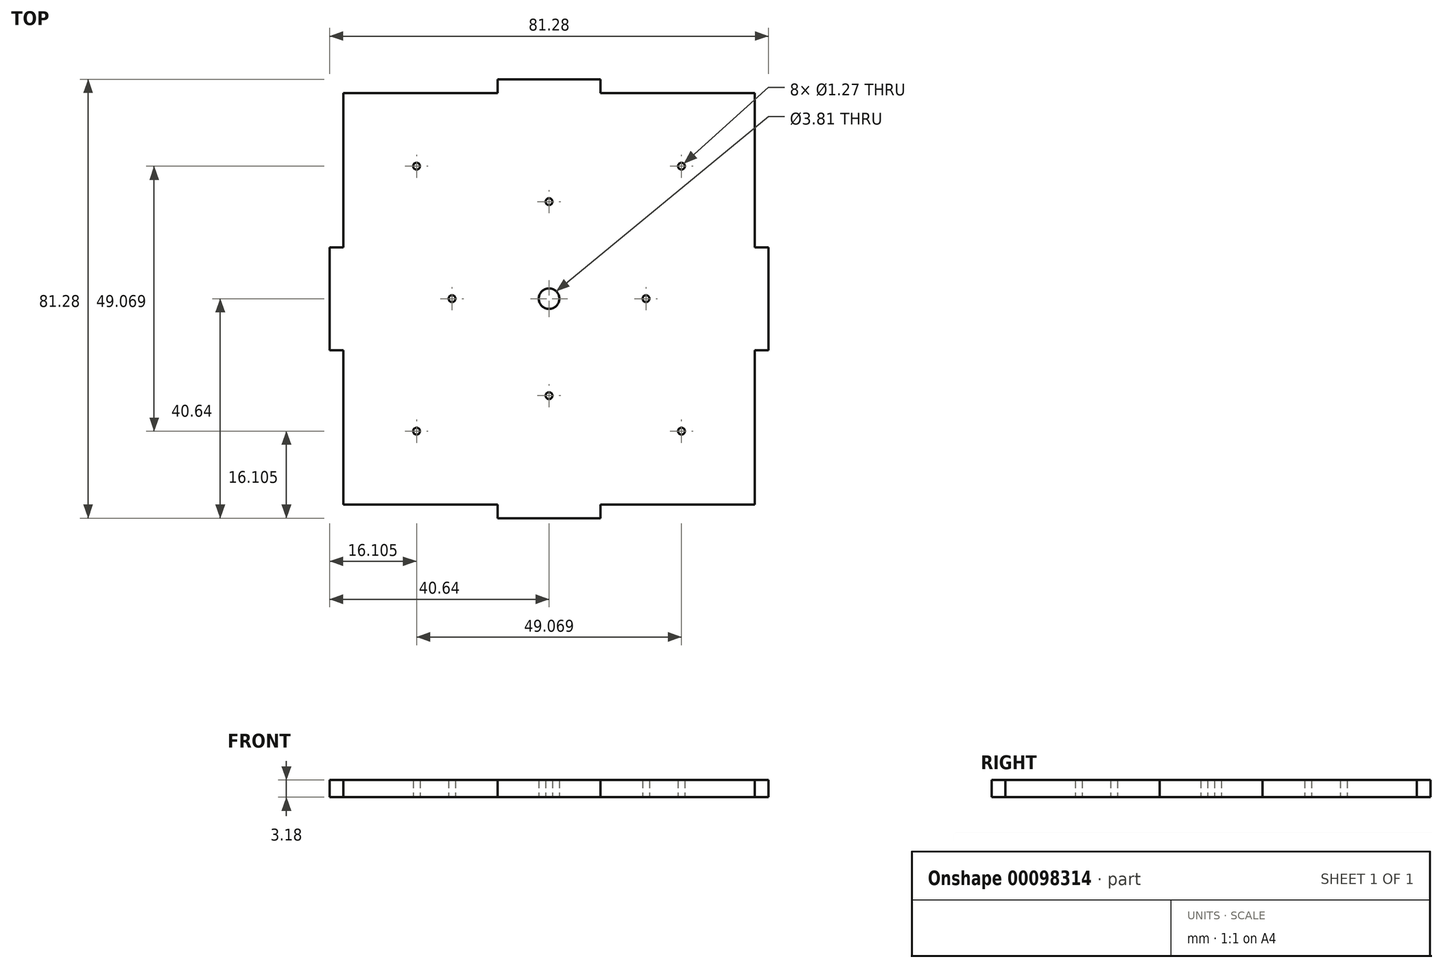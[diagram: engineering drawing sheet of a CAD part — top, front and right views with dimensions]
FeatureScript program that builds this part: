
annotation { "Feature Type Name" : "Feature", "Feature Type Description" : "" }
export const myFeature = defineFeature(function(context is Context, id is Id, definition is map)
    precondition{}
    {
        {
            var Q0;
            Q0=qCreatedBy(makeId("Top.planeOp"),FACE);
            var sketch = newSketch(context, id + "F0", { "sketchPlane" : qUnion([Q0])});
            skCircle(sketch, "E0", {"center": v(0, 17.96) * mm, "radius": 6.99 * mm, "construction": true});
            skCircle(sketch, "E1", {"center": v(-17.96, 0) * mm, "radius": 6.99 * mm, "construction": true});
            skCircle(sketch, "E2", {"center": v(0, -17.96) * mm, "radius": 6.99 * mm, "construction": true});
            skCircle(sketch, "E3", {"center": v(17.96, 0) * mm, "radius": 6.99 * mm, "construction": true});
            skCircle(sketch, "E4", {"center": v(24.53, 24.53) * mm, "radius": 6.99 * mm, "construction": true});
            skCircle(sketch, "E5", {"center": v(-24.53, 24.53) * mm, "radius": 6.99 * mm, "construction": true});
            skCircle(sketch, "E6", {"center": v(-24.53, -24.53) * mm, "radius": 6.99 * mm, "construction": true});
            skCircle(sketch, "E7", {"center": v(24.53, -24.53) * mm, "radius": 6.99 * mm, "construction": true});
            skLineSegment(sketch, "E8", {"start": v(-17.96, 0) * mm, "end": v(0, 17.96) * mm, "construction": true});
            skLineSegment(sketch, "E9", {"start": v(17.96, 0) * mm, "end": v(0, 17.96) * mm, "construction": true});
            skLineSegment(sketch, "E10", {"start": v(0, -17.96) * mm, "end": v(-17.96, 0) * mm, "construction": true});
            skLineSegment(sketch, "E11", {"start": v(0, -17.96) * mm, "end": v(17.96, 0) * mm, "construction": true});
            skLineSegment(sketch, "E12", {"start": v(-24.53, -24.53) * mm, "end": v(24.53, 24.53) * mm, "construction": true});
            skLineSegment(sketch, "E13", {"start": v(-24.53, 24.53) * mm, "end": v(24.53, -24.53) * mm, "construction": true});
            skLineSegment(sketch, "E14", {"start": v(0, 17.96) * mm, "end": v(24.53, 24.53) * mm, "construction": true});
            skLineSegment(sketch, "E15", {"start": v(-38.1, 38.1) * mm, "end": v(-9.53, 38.1) * mm});
            skLineSegment(sketch, "E16", {"start": v(-9.52, 38.1) * mm, "end": v(-9.52, 40.64) * mm});
            skLineSegment(sketch, "E17", {"start": v(-9.53, 40.64) * mm, "end": v(9.52, 40.64) * mm});
            skLineSegment(sketch, "E18", {"start": v(9.53, 40.64) * mm, "end": v(9.53, 38.1) * mm});
            skLineSegment(sketch, "E19", {"start": v(9.53, 38.1) * mm, "end": v(38.1, 38.1) * mm});
            skLineSegment(sketch, "E20", {"start": v(38.1, 38.1) * mm, "end": v(38.1, 9.53) * mm});
            skLineSegment(sketch, "E21", {"start": v(38.1, 9.53) * mm, "end": v(40.64, 9.53) * mm});
            skLineSegment(sketch, "E22", {"start": v(40.64, 9.53) * mm, "end": v(40.64, -9.52) * mm});
            skLineSegment(sketch, "E23", {"start": v(40.64, -9.52) * mm, "end": v(38.1, -9.52) * mm});
            skLineSegment(sketch, "E24", {"start": v(38.1, -9.52) * mm, "end": v(38.1, -38.1) * mm});
            skLineSegment(sketch, "E25", {"start": v(38.1, -38.1) * mm, "end": v(9.53, -38.1) * mm});
            skLineSegment(sketch, "E26", {"start": v(9.53, -38.1) * mm, "end": v(9.53, -40.64) * mm});
            skLineSegment(sketch, "E27", {"start": v(9.52, -40.64) * mm, "end": v(-9.53, -40.64) * mm});
            skLineSegment(sketch, "E28", {"start": v(-9.52, -40.64) * mm, "end": v(-9.52, -38.1) * mm});
            skLineSegment(sketch, "E29", {"start": v(-9.53, -38.1) * mm, "end": v(-38.1, -38.1) * mm});
            skLineSegment(sketch, "E30", {"start": v(-38.1, -38.1) * mm, "end": v(-38.1, -9.52) * mm});
            skLineSegment(sketch, "E31", {"start": v(-38.1, -9.52) * mm, "end": v(-40.64, -9.52) * mm});
            skLineSegment(sketch, "E32", {"start": v(-40.64, -9.52) * mm, "end": v(-40.64, 9.53) * mm});
            skLineSegment(sketch, "E33", {"start": v(-40.64, 9.53) * mm, "end": v(-38.1, 9.53) * mm});
            skLineSegment(sketch, "E34", {"start": v(-38.1, 9.53) * mm, "end": v(-38.1, 38.1) * mm});
            skCircle(sketch, "E35", {"center": v(0, 0) * mm, "radius": 1.9 * mm});
            skCircle(sketch, "E36", {"center": v(-24.53, 24.53) * mm, "radius": 0.64 * mm});
            skCircle(sketch, "E37", {"center": v(0, 17.96) * mm, "radius": 0.64 * mm});
            skCircle(sketch, "E38", {"center": v(24.53, 24.53) * mm, "radius": 0.64 * mm});
            skCircle(sketch, "E39", {"center": v(17.96, 0) * mm, "radius": 0.64 * mm});
            skCircle(sketch, "E40", {"center": v(-17.96, 0) * mm, "radius": 0.64 * mm});
            skCircle(sketch, "E41", {"center": v(-24.53, -24.53) * mm, "radius": 0.64 * mm});
            skCircle(sketch, "E42", {"center": v(0, -17.96) * mm, "radius": 0.64 * mm});
            skCircle(sketch, "E43", {"center": v(24.53, -24.53) * mm, "radius": 0.64 * mm});
            skSolve(sketch);
        }
        {
            var Q0;
            Q0 = qSketchRegion(id + "F0", true);
            extrude(context, id + "F1", {"entities" : qUnion([Q0]), "depth" : 3.17 * mm});
        }
    });
